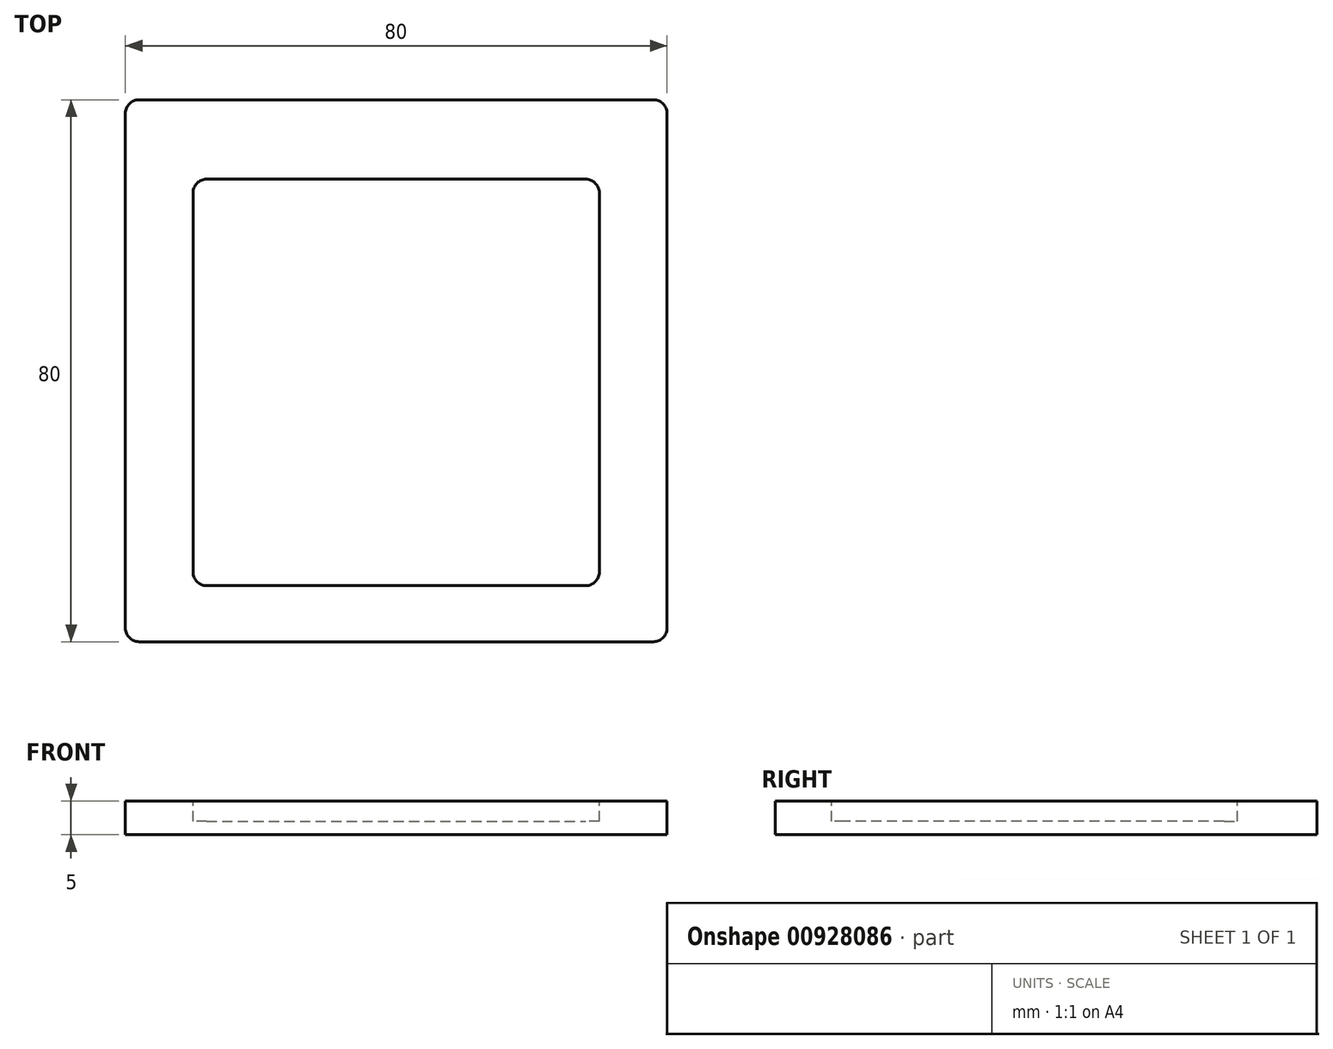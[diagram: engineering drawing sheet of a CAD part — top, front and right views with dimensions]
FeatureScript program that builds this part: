
annotation { "Feature Type Name" : "Feature", "Feature Type Description" : "" }
export const myFeature = defineFeature(function(context is Context, id is Id, definition is map)
    precondition{}
    {
        {
            var Q0;
            Q0=qCreatedBy(makeId("Top.planeOp"),FACE);
            var sketch = newSketch(context, id + "F0", { "sketchPlane" : qUnion([Q0])});
            skLineSegment(sketch, "E0.bottom", {"start": v(-38, 40) * mm, "end": v(38, 40) * mm});
            skLineSegment(sketch, "E0.top", {"start": v(-38, -40) * mm, "end": v(38, -40) * mm});
            skLineSegment(sketch, "E0.left", {"start": v(-40, 38) * mm, "end": v(-40, -38) * mm});
            skLineSegment(sketch, "E0.right", {"start": v(40, 38) * mm, "end": v(40, -38) * mm});
            skPoint(sketch, "E0.middle", {"position": v(0, 0) * mm});
            skPoint(sketch, "E1.visualSharp", {"position": v(-40, 40) * mm});
            skArc(sketch, "E1.filletArc", {"start": v(-38, 40) * mm, "mid": v(-39.41, 39.41) * mm, "end": v(-40, 38) * mm});
            skPoint(sketch, "E2.visualSharp", {"position": v(40, 40) * mm});
            skArc(sketch, "E2.filletArc", {"start": v(40, 38) * mm, "mid": v(39.41, 39.41) * mm, "end": v(38, 40) * mm});
            skPoint(sketch, "E3.visualSharp", {"position": v(40, -40) * mm});
            skArc(sketch, "E3.filletArc", {"start": v(38, -40) * mm, "mid": v(39.41, -39.41) * mm, "end": v(40, -38) * mm});
            skPoint(sketch, "E4.visualSharp", {"position": v(-40, -40) * mm});
            skArc(sketch, "E4.filletArc", {"start": v(-40, -38) * mm, "mid": v(-39.41, -39.41) * mm, "end": v(-38, -40) * mm});
            skSolve(sketch);
        }
        {
            var Q0;
            Q0=makeQuery(id+"F0.imprint","IMPRINT",FACE,{"disambiguationData":[TD([[makeQuery(id+"F0.imprint","IMPRINT",EDGE,{"derivedFrom":sQuery(id+"F0.wireOp",EDGE,"E0.bottom")}),-1.0]])]});
            extrude(context, id + "F1", {"entities" : qUnion([Q0]), "depth" : 5 * mm, "offsetDistance" : 25 * mm});
        }
        {
            var Q0;
            Q0=makeQuery(id+"F1.opExtrude","CAP_FACE",FACE,{"disambiguationData":[OSD([sQuery(id+"F0.wireOp",EDGE,"E0.bottom"),sQuery(id+"F0.wireOp",EDGE,"E0.top"),sQuery(id+"F0.wireOp",EDGE,"E0.left"),sQuery(id+"F0.wireOp",EDGE,"E0.right"),sQuery(id+"F0.wireOp",EDGE,"E1.filletArc"),sQuery(id+"F0.wireOp",EDGE,"E2.filletArc"),sQuery(id+"F0.wireOp",EDGE,"E3.filletArc"),sQuery(id+"F0.wireOp",EDGE,"E4.filletArc")])],"isStart":false});
            var sketch = newSketch(context, id + "F2", { "sketchPlane" : qUnion([Q0])});
            skLineSegment(sketch, "E5.bottom", {"start": v(-28, 28.28) * mm, "end": v(28, 28.28) * mm});
            skLineSegment(sketch, "E5.top", {"start": v(-28, -31.72) * mm, "end": v(28, -31.72) * mm});
            skLineSegment(sketch, "E5.left", {"start": v(-30, 26.28) * mm, "end": v(-30, -29.72) * mm});
            skLineSegment(sketch, "E5.right", {"start": v(30, 26.28) * mm, "end": v(30, -29.72) * mm});
            skPoint(sketch, "E5.middle", {"position": v(0, -1.72) * mm});
            skPoint(sketch, "E6.visualSharp", {"position": v(-30, 28.28) * mm});
            skArc(sketch, "E6.filletArc", {"start": v(-28, 28.28) * mm, "mid": v(-29.41, 27.7) * mm, "end": v(-30, 26.28) * mm});
            skPoint(sketch, "E7.visualSharp", {"position": v(30, 28.28) * mm});
            skArc(sketch, "E7.filletArc", {"start": v(30, 26.28) * mm, "mid": v(29.41, 27.7) * mm, "end": v(28, 28.28) * mm});
            skPoint(sketch, "E8.visualSharp", {"position": v(30, -31.72) * mm});
            skArc(sketch, "E8.filletArc", {"start": v(28, -31.72) * mm, "mid": v(29.41, -31.14) * mm, "end": v(30, -29.72) * mm});
            skPoint(sketch, "E9.visualSharp", {"position": v(-30, -31.72) * mm});
            skArc(sketch, "E9.filletArc", {"start": v(-30, -29.72) * mm, "mid": v(-29.41, -31.14) * mm, "end": v(-28, -31.72) * mm});
            skSolve(sketch);
        }
        {
            var Q0;
            Q0=makeQuery(id+"F2.imprint","IMPRINT",FACE,{"disambiguationData":[TD([[makeQuery(id+"F2.imprint","IMPRINT",EDGE,{"derivedFrom":sQuery(id+"F2.wireOp",EDGE,"E5.bottom")}),-1.0]])]});
            extrude(context, id + "F3", {"entities" : qUnion([Q0]), "operationType" : NewBodyOperationType.REMOVE, "oppositeDirection" : true, "depth" : 3 * mm, "offsetDistance" : 25 * mm});
        }
    });
